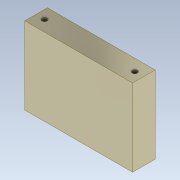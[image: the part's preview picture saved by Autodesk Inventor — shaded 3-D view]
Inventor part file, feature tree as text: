
AUTODESK INVENTOR PART (.ipt)
format: ipt  version: 2022 (Build 260153000, 153)  size: 139,264 bytes
history: native  units: mm
features: extrude x2, thread x2, sketch x2
ambient origin geometry x8: Origin, YZ Plane, XZ Plane, XY Plane, X Axis, Y Axis, Z Axis, Center Point
bodies: Solid1 (feature_tree)
feature tree (6):
  extrude  "Extrusion1"  Depth=26.0mm
  extrude  "Extrusion2"  Depth=124.000203mm
  thread  "Thread1"  [1 undecoded]
  thread  "Thread2"  [1 undecoded]
  sketch  "Sketch1"  dims[d0=124.0mm d1=26.0mm]
  sketch  "Sketch2"  dims[d2=89.0mm d3=0.0mm d4=124.000203mm d5=26.0mm d6=124.0mm d7=26.0mm d8=124.000203mm d9=26.0mm d10=10.0mm d11=0.0mm d12=10.0mm d13=0.0mm d14=10.0mm d15=0.0mm]
note: 2 required parameter values undecoded (feature->parameter linkage not recoverable at this tier; creation-order binding heuristic only, values carry confidence <= 0.55)
